# Revit family: Solido Smart cistilna naprava - Beton
name_source: partatom
category: Specialty Equipment
revit_build: Autodesk Revit Architecture 2015 (Build: 20140606_1530(x64)
units: mm (PartAtom-declared; Revit-internal decimal feet)

## types (3) — shared parameters
Description = Biološka čistilna naprava Solido SMART v betonskem rezervoarju (2 do 10 PE)
Diameter = 2240 mm  [stored 7.34908 ft]
GZS list of Water Treatement Plant = https://www.gzs.si
Instalation Instructions = http://gorec.info
Manufacturer = Gorec
Manufacturer Website = http://www.gorec.info
Material = Concrete, Precast
Note = Vtočna cev fi110, fi125, fi160.
Pipe Diameter = 110 mm  [stored 0.360892 ft]
Product Certification = SIST EN 12566-3
Pump Type = Kompresorska zračna črpalka
URL = http://gorec.info
Voltage = 220 $
You Tube = https://www.youtube.com

## per-type parameters (varying)
| type | Height | Max. Daily Water Flow (l) | Model | Volume | Weight |
| 2 do 5 PE | 2190 mm  [stored 7.18504 ft] | 750 | MBČN Solido SMART CBE 2 do 5pe | 3750 m³ | 4300.00 kg |
| 6 do 8 PE | 2620 mm  [stored 8.5958 ft] | 1200 | MBČN Solido SMART CBE 6 do 8pe | 5000 m³ | 5500.00 kg |
| 9 do 10 PE | 3090 mm | 1500 | MBČN Solido SMART EBE 9 do 10pe | 6600 m³ | 6400.00 kg |

note: [stored X ft] marks values corroborated as IEEE doubles in the binary element streams (Revit-internal decimal feet)

## geometry (parser evidence)
native form markers: Blend x18, Sweep x25
no freeform markers — native parametric forms only
